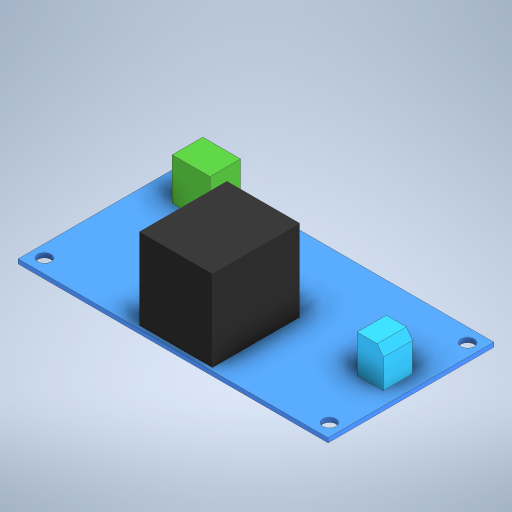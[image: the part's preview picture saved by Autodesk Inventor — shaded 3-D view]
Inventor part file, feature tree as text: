
AUTODESK INVENTOR PART (.ipt)
format: ipt  version: 2023 (Build 270158000, 158)  size: 300,544 bytes
history: native  units: mm
features: extrude x4, sketch x4, other x1
ambient origin geometry x8: Origin, YZ Plane, XZ Plane, XY Plane, X Axis, Y Axis, Z Axis, Center Point
bodies: Body1 (feature_tree)
feature tree (9):
  other  "솔리드1"
  extrude  "돌출1"  Depth=106.6mm
  extrude  "돌출2"  Depth=57.0mm
  extrude  "돌출3"  Depth=4.5mm
  extrude  "돌출4"  Depth=47.5mm
  sketch  "스케치1"
  sketch  "스케치2"
  sketch  "스케치3"
  sketch  "스케치4"
